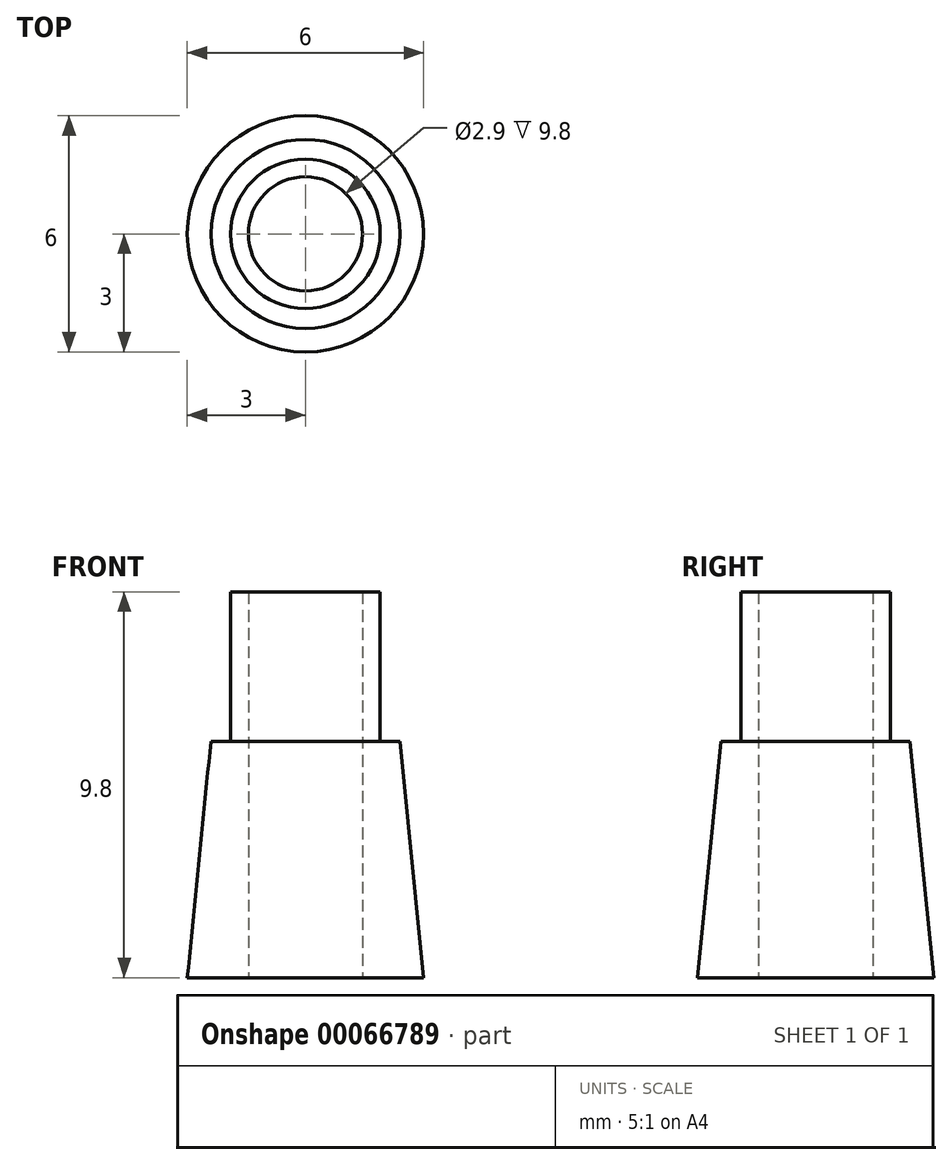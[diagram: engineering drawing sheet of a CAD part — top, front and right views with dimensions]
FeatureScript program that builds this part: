
annotation { "Feature Type Name" : "Feature", "Feature Type Description" : "" }
export const myFeature = defineFeature(function(context is Context, id is Id, definition is map)
    precondition{}
    {
        {
            var Q0;
            Q0=qCreatedBy(makeId("Front.planeOp"),FACE);
            var sketch = newSketch(context, id + "F0", { "sketchPlane" : qUnion([Q0])});
            skLineSegment(sketch, "E0", {"start": v(1.45, 0) * mm, "end": v(1.45, 9.8) * mm});
            skLineSegment(sketch, "E1", {"start": v(1.45, 9.8) * mm, "end": v(1.9, 9.8) * mm});
            skLineSegment(sketch, "E2", {"start": v(1.9, 9.8) * mm, "end": v(1.9, 6) * mm});
            skLineSegment(sketch, "E3", {"start": v(1.9, 6) * mm, "end": v(2.4, 6) * mm});
            skLineSegment(sketch, "E4", {"start": v(2.4, 6) * mm, "end": v(3, 0) * mm});
            skLineSegment(sketch, "E5", {"start": v(3, 0) * mm, "end": v(1.45, 0) * mm});
            skLineSegment(sketch, "E6", {"start": v(0, 0) * mm, "end": v(0, 14.76) * mm});
            skSolve(sketch);
        }
        {
            var Q0;
            Q0=makeQuery(id+"F0.imprint","IMPRINT",FACE,{"disambiguationData":[TD([[makeQuery(id+"F0.imprint","IMPRINT",EDGE,{"derivedFrom":sQuery(id+"F0.wireOp",EDGE,"E0")}),-1.0]])]});
            var Q1;
            Q1=sQuery(id+"F0.wireOp",EDGE,"E6");
            revolve(context, id + "F1", {"entities" : qUnion([Q0]), "axis" : qUnion([Q1]), "revolveType" : RevolveType.FULL});
        }
    });
